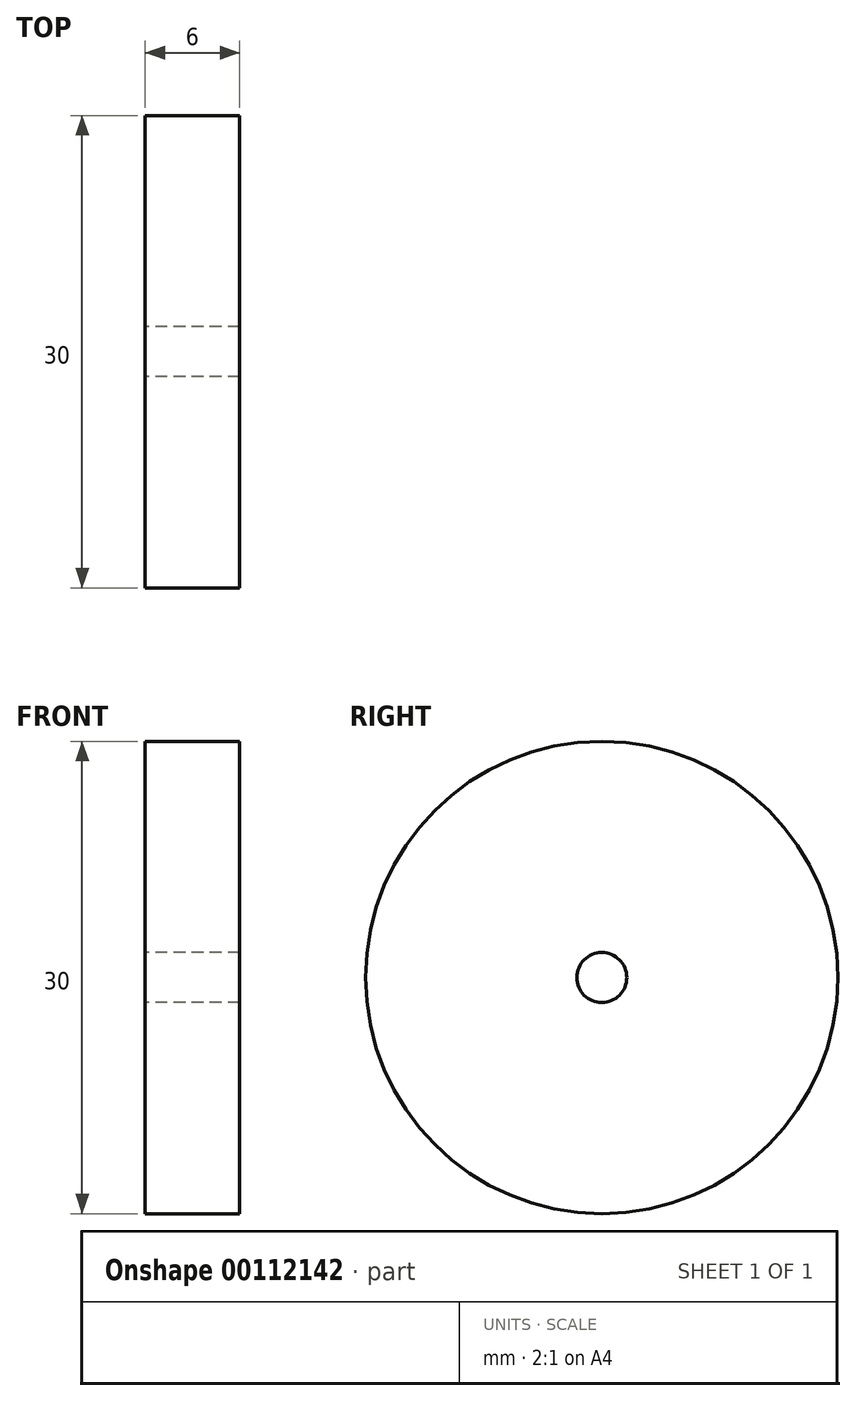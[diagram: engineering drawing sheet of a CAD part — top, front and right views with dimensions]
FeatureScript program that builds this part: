
annotation { "Feature Type Name" : "Feature", "Feature Type Description" : "" }
export const myFeature = defineFeature(function(context is Context, id is Id, definition is map)
    precondition{}
    {
        {
            var Q0;
            Q0=qCreatedBy(makeId("Right.planeOp"),FACE);
            var sketch = newSketch(context, id + "F0", { "sketchPlane" : qUnion([Q0])});
            skCircle(sketch, "E0", {"center": v(0, 0) * mm, "radius": 15 * mm});
            skCircle(sketch, "E1", {"center": v(0, 0) * mm, "radius": 1.59 * mm});
            skSolve(sketch);
        }
        {
            var Q0;
            Q0 = qSketchRegion(id + "F0", true);
            extrude(context, id + "F1", {"entities" : qUnion([Q0]), "depth" : 6 * mm});
        }
    });
